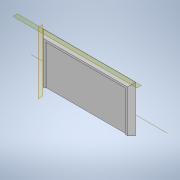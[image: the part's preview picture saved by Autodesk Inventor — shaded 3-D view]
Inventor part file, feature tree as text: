
AUTODESK INVENTOR PART (.ipt)
format: ipt  version: 2022 (Build 260153000, 153)  size: 116,224 bytes
history: native  units: mm
features: plane x2, sketch x2, extrude x2, other x1, chamfer x1
ambient origin geometry x8: Origin, YZ Plane, XZ Plane, XY Plane, X Axis, Y Axis, Z Axis, Center Point
bodies: Solid1 (feature_tree)
feature tree (8):
  plane  "Work Plane1"
  sketch  "Sketch2"  dims[d10=45.0deg d11=2.0mm d12=12.7mm d13=90.0deg d16=90.0deg d17=88.9mm]
  other  "Work Axis1"
  plane  "Work Plane2"
  sketch  "Sketch1"  dims[d0=19.05mm d1=19.05mm d2=254.0mm d3=127.0mm d5=0.0mm d6=12.7mm d8=0.0mm d9=9.525mm]
  extrude  "Extrusion1"  Depth=9.525mm TaperAngle=0.0deg
  extrude  "Extrusion2"  TaperAngle=90.0deg  [1 undecoded]
  chamfer  "Chamfer1"  Distance=88.9mm Angle=90.0deg
note: 1 required parameter value undecoded (feature->parameter linkage not recoverable at this tier; creation-order binding heuristic only, values carry confidence <= 0.55)
